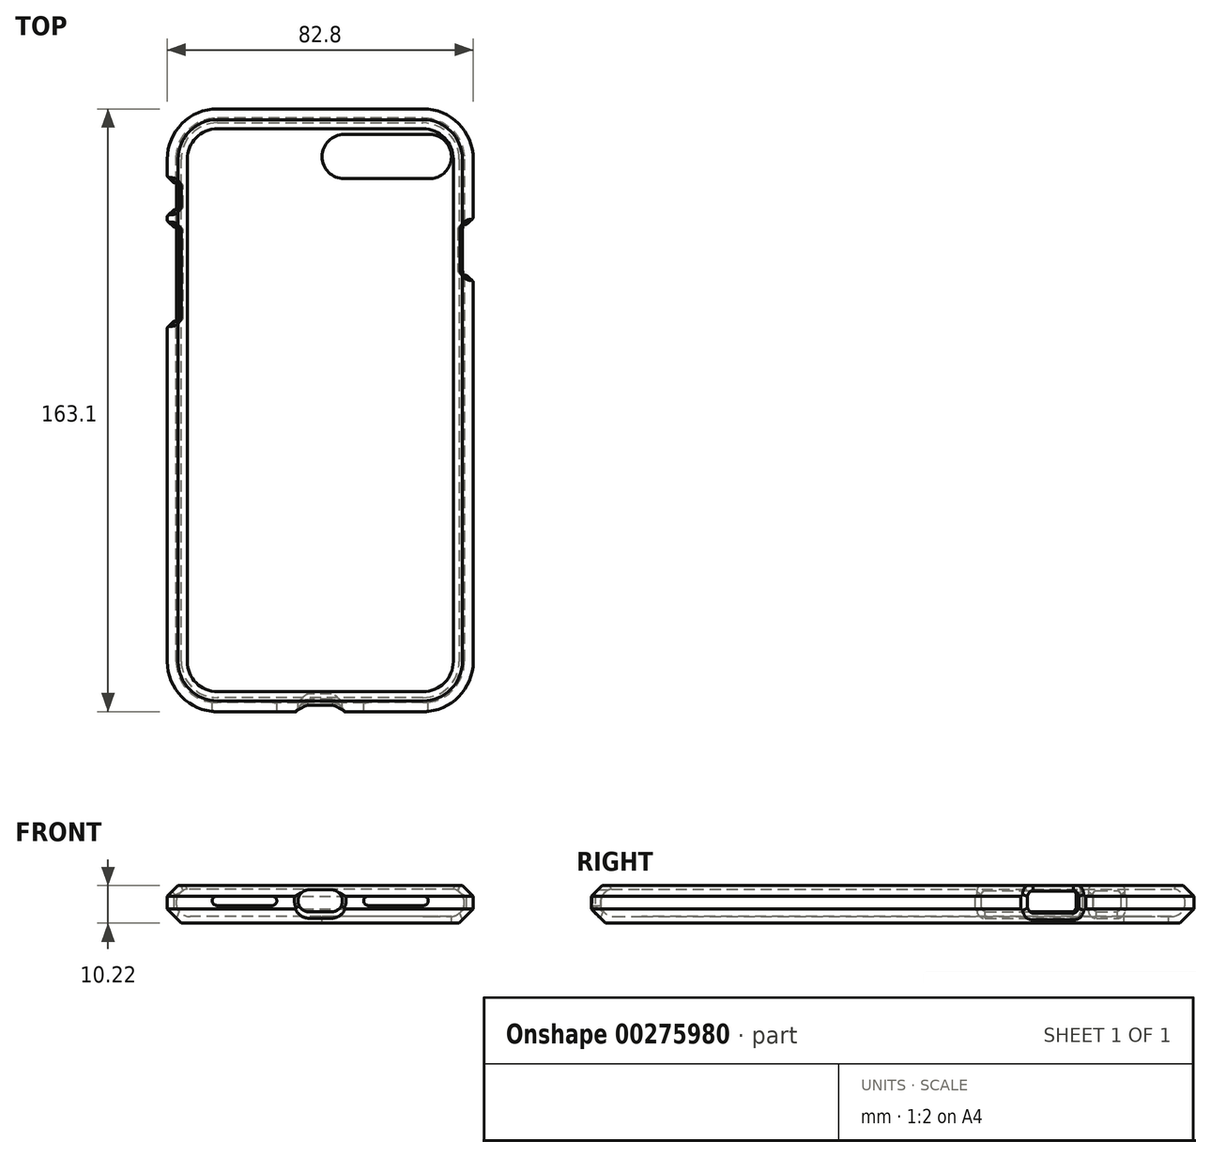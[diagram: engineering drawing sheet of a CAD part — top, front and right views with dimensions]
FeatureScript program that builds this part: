
annotation { "Feature Type Name" : "Feature", "Feature Type Description" : "" }
export const myFeature = defineFeature(function(context is Context, id is Id, definition is map)
    precondition{}
    {
        {
            assignVariable(context, id + "F0", {"name" : "HoleChamferLength", "anyValue" : 1.25});
        }
        {
            assignVariable(context, id + "F1", {"name" : "HoleChamferTopBottom", "anyValue" : 1.75});
        }
        {
            var Q0;
            Q0=qCreatedBy(makeId("Top.planeOp"),FACE);
            var sketch = newSketch(context, id + "F2", { "sketchPlane" : qUnion([Q0])});
            skLineSegment(sketch, "E0.bottom", {"start": v(27.8, 79.15) * mm, "end": v(0, 79.15) * mm});
            skLineSegment(sketch, "E0.top", {"start": v(27.8, -79.15) * mm, "end": v(-27.8, -79.15) * mm});
            skLineSegment(sketch, "E0.left", {"start": v(39, 67.95) * mm, "end": v(39, -67.95) * mm});
            skLineSegment(sketch, "E0.right", {"start": v(-39, 67.95) * mm, "end": v(-39, -67.95) * mm});
            skPoint(sketch, "E0.middle", {"position": v(0, 0) * mm});
            skPoint(sketch, "E1.visualSharp", {"position": v(-39, 79.15) * mm});
            skArc(sketch, "E1.filletArc", {"start": v(-27.8, 79.15) * mm, "mid": v(-35.72, 75.87) * mm, "end": v(-39, 67.95) * mm});
            skPoint(sketch, "E2.visualSharp", {"position": v(39, 79.15) * mm});
            skArc(sketch, "E2.filletArc", {"start": v(39, 67.95) * mm, "mid": v(35.72, 75.87) * mm, "end": v(27.8, 79.15) * mm});
            skPoint(sketch, "E3.visualSharp", {"position": v(39, -79.15) * mm});
            skArc(sketch, "E3.filletArc", {"start": v(27.8, -79.15) * mm, "mid": v(35.72, -75.87) * mm, "end": v(39, -67.95) * mm});
            skPoint(sketch, "E4.visualSharp", {"position": v(-39, -79.15) * mm});
            skArc(sketch, "E4.filletArc", {"start": v(-39, -67.95) * mm, "mid": v(-35.72, -75.87) * mm, "end": v(-27.8, -79.15) * mm});
            skLineSegment(sketch, "E5", {"start": v(0, 79.15) * mm, "end": v(-27.8, 79.15) * mm});
            skSolve(sketch);
        }
        {
            var Q0;
            Q0=qCreatedBy(makeId("Right.planeOp"),FACE);
            var sketch = newSketch(context, id + "F3", { "sketchPlane" : qUnion([Q0])});
            skPoint(sketch, "E6.0", {"position": v(79.15, 0) * mm});
            skArc(sketch, "E7", {"start": v(75.4, -3.75) * mm, "mid": v(79.15, 0) * mm, "end": v(75.4, 3.75) * mm});
            skLineSegment(sketch, "E8", {"start": v(75.4, -3.75) * mm, "end": v(75.4, 3.75) * mm, "construction": true});
            skLineSegment(sketch, "E9", {"start": v(81.55, -1.75) * mm, "end": v(81.55, 1.75) * mm});
            skLineSegment(sketch, "E10", {"start": v(81.55, 1.75) * mm, "end": v(79.77, 3.53) * mm});
            skLineSegment(sketch, "E11.trimOffspring", {"start": v(79.77, -3.53) * mm, "end": v(81.55, -1.75) * mm});
            skLineSegment(sketch, "E12", {"start": v(75.4, -5.55) * mm, "end": v(75.4, -3.75) * mm});
            skLineSegment(sketch, "E13", {"start": v(75.4, -5.55) * mm, "end": v(84.8, -5.55) * mm, "construction": true});
            skPoint(sketch, "E14", {"position": v(81.55, 0) * mm});
            skPoint(sketch, "E15.visualSharp", {"position": v(66.64, 4.65) * mm});
            skArc(sketch, "E15.filletArc", {"start": v(77.37, 4.67) * mm, "mid": v(76.58, 4.4) * mm, "end": v(76.15, 3.67) * mm});
            skLineSegment(sketch, "E16", {"start": v(79.77, -3.53) * mm, "end": v(77.75, -5.55) * mm});
            skLineSegment(sketch, "E17", {"start": v(77.75, -5.55) * mm, "end": v(75.4, -5.55) * mm});
            skLineSegment(sketch, "E18", {"start": v(79.77, 3.53) * mm, "end": v(78.63, 4.67) * mm});
            skLineSegment(sketch, "E19", {"start": v(78.63, 4.67) * mm, "end": v(77.37, 4.67) * mm});
            skLineSegment(sketch, "E20", {"start": v(76.15, 3.67) * mm, "end": v(68.38, 5.26) * mm, "construction": true});
            skSolve(sketch);
        }
        {
            var Q0;
            Q0=sQuery(id+"F2.wireOp",EDGE,"E5");
            var Q1;
            Q1=sQuery(id+"F2.wireOp",VERTEX,"E5.end");
            cPlane(context, id + "F4", {"entities" : qUnion([Q0, Q1]), "cplaneType" : CPlaneType.LINE_POINT, "offset" : 25 * mm, "width" : 150 * mm, "height" : 150 * mm});
        }
        {
            var Q0;
            Q0=sQuery(id+"F2.wireOp",EDGE,"E0.bottom");
            var Q1;
            Q1=sQuery(id+"F2.wireOp",VERTEX,"E2.filletArc.end");
            cPlane(context, id + "F5", {"entities" : qUnion([Q0, Q1]), "cplaneType" : CPlaneType.LINE_POINT, "offset" : 25 * mm, "width" : 150 * mm, "height" : 150 * mm});
        }
        {
            var Q0;
            Q0=sQuery(id+"F2.wireOp",EDGE,"E0.right");
            var Q1;
            Q1=sQuery(id+"F2.wireOp",VERTEX,"E0.right.end");
            cPlane(context, id + "F6", {"entities" : qUnion([Q0, Q1]), "cplaneType" : CPlaneType.LINE_POINT, "offset" : 25 * mm, "width" : 150 * mm, "height" : 150 * mm});
        }
        {
            var Q0;
            Q0=qCreatedBy(id+"F4.planeOp",FACE);
            var sketch = newSketch(context, id + "F7", { "sketchPlane" : qUnion([Q0])});
            skLineSegment(sketch, "E21.bottom", {"start": v(-25, -2.13) * mm, "end": v(-48.65, -2.13) * mm});
            skLineSegment(sketch, "E21.top", {"start": v(-25, 3.12) * mm, "end": v(-48.65, 3.12) * mm});
            skLineSegment(sketch, "E21.left", {"start": v(-24, -1.13) * mm, "end": v(-24, 2.12) * mm});
            skLineSegment(sketch, "E21.right", {"start": v(-49.65, -1.13) * mm, "end": v(-49.65, 2.12) * mm});
            skPoint(sketch, "E21.middle", {"position": v(-36.82, 0.5) * mm});
            skPoint(sketch, "E22.visualSharp", {"position": v(-49.65, 3.12) * mm});
            skArc(sketch, "E22.filletArc", {"start": v(-48.65, 3.12) * mm, "mid": v(-49.36, 2.83) * mm, "end": v(-49.65, 2.12) * mm});
            skPoint(sketch, "E23.visualSharp", {"position": v(-49.65, -2.13) * mm});
            skArc(sketch, "E23.filletArc", {"start": v(-49.65, -1.13) * mm, "mid": v(-49.36, -1.83) * mm, "end": v(-48.65, -2.13) * mm});
            skPoint(sketch, "E24.visualSharp", {"position": v(-24, 3.12) * mm});
            skArc(sketch, "E24.filletArc", {"start": v(-24, 2.12) * mm, "mid": v(-24.3, 2.83) * mm, "end": v(-25, 3.12) * mm});
            skPoint(sketch, "E25.visualSharp", {"position": v(-24, -2.12) * mm});
            skArc(sketch, "E25.filletArc", {"start": v(-25, -2.12) * mm, "mid": v(-24.3, -1.83) * mm, "end": v(-24, -1.13) * mm});
            skLineSegment(sketch, "E26.bottom", {"start": v(-60.65, 3.12) * mm, "end": v(-55.15, 3.12) * mm});
            skLineSegment(sketch, "E26.top", {"start": v(-60.65, -2.13) * mm, "end": v(-55.15, -2.13) * mm});
            skLineSegment(sketch, "E26.left", {"start": v(-61.65, 2.12) * mm, "end": v(-61.65, -1.13) * mm});
            skLineSegment(sketch, "E26.right", {"start": v(-54.15, 2.12) * mm, "end": v(-54.15, -1.13) * mm});
            skPoint(sketch, "E26.middle", {"position": v(-57.9, 0.5) * mm});
            skPoint(sketch, "E27.visualSharp", {"position": v(-61.65, 3.12) * mm});
            skArc(sketch, "E27.filletArc", {"start": v(-60.65, 3.13) * mm, "mid": v(-61.36, 2.83) * mm, "end": v(-61.65, 2.12) * mm});
            skPoint(sketch, "E28.visualSharp", {"position": v(-61.65, -2.13) * mm});
            skArc(sketch, "E28.filletArc", {"start": v(-61.65, -1.13) * mm, "mid": v(-61.36, -1.83) * mm, "end": v(-60.65, -2.13) * mm});
            skPoint(sketch, "E29.visualSharp", {"position": v(-54.15, -2.13) * mm});
            skArc(sketch, "E29.filletArc", {"start": v(-55.15, -2.13) * mm, "mid": v(-54.44, -1.83) * mm, "end": v(-54.15, -1.13) * mm});
            skPoint(sketch, "E30.visualSharp", {"position": v(-54.15, 3.12) * mm});
            skArc(sketch, "E30.filletArc", {"start": v(-54.15, 2.12) * mm, "mid": v(-54.44, 2.83) * mm, "end": v(-55.15, 3.13) * mm});
            skSolve(sketch);
        }
        {
            var Q0;
            Q0=qCreatedBy(id+"F5.planeOp",FACE);
            var sketch = newSketch(context, id + "F8", { "sketchPlane" : qUnion([Q0])});
            skLineSegment(sketch, "E31.bottom", {"start": v(-48.9, 3) * mm, "end": v(-37.9, 3) * mm});
            skLineSegment(sketch, "E31.top", {"start": v(-48.9, -2.5) * mm, "end": v(-37.9, -2.5) * mm});
            skLineSegment(sketch, "E31.left", {"start": v(-50.4, 1.5) * mm, "end": v(-50.4, -1) * mm});
            skLineSegment(sketch, "E31.right", {"start": v(-36.4, 1.5) * mm, "end": v(-36.4, -1) * mm});
            skPoint(sketch, "E31.middle", {"position": v(-43.4, 0.25) * mm});
            skPoint(sketch, "E32.visualSharp", {"position": v(-50.4, 3) * mm});
            skArc(sketch, "E32.filletArc", {"start": v(-48.9, 3) * mm, "mid": v(-49.96, 2.56) * mm, "end": v(-50.4, 1.5) * mm});
            skPoint(sketch, "E33.visualSharp", {"position": v(-50.4, -2.5) * mm});
            skArc(sketch, "E33.filletArc", {"start": v(-50.4, -1) * mm, "mid": v(-49.96, -2.06) * mm, "end": v(-48.9, -2.5) * mm});
            skPoint(sketch, "E34.visualSharp", {"position": v(-36.4, -2.5) * mm});
            skArc(sketch, "E34.filletArc", {"start": v(-37.9, -2.5) * mm, "mid": v(-36.84, -2.06) * mm, "end": v(-36.4, -1) * mm});
            skPoint(sketch, "E35.visualSharp", {"position": v(-36.4, 3) * mm});
            skArc(sketch, "E35.filletArc", {"start": v(-36.4, 1.5) * mm, "mid": v(-36.84, 2.56) * mm, "end": v(-37.9, 3) * mm});
            skSolve(sketch);
        }
        {
            var Q0;
            Q0=qCreatedBy(id+"F6.planeOp",FACE);
            var sketch = newSketch(context, id + "F9", { "sketchPlane" : qUnion([Q0])});
            skLineSegment(sketch, "E36.bottom", {"start": v(3, 3.5) * mm, "end": v(-3, 3.5) * mm});
            skLineSegment(sketch, "E36.top", {"start": v(3, -2.5) * mm, "end": v(-3, -2.5) * mm});
            skLineSegment(sketch, "E36.left", {"start": v(6, 0.5) * mm, "end": v(6, 0.5) * mm});
            skLineSegment(sketch, "E36.right", {"start": v(-6, 0.5) * mm, "end": v(-6, 0.5) * mm});
            skPoint(sketch, "E36.middle", {"position": v(0, 0.5) * mm});
            skPoint(sketch, "E37.visualSharp", {"position": v(-6, 3.5) * mm});
            skArc(sketch, "E37.filletArc", {"start": v(-3, 3.5) * mm, "mid": v(-5.12, 2.62) * mm, "end": v(-6, 0.5) * mm});
            skPoint(sketch, "E38.visualSharp", {"position": v(-6, -2.5) * mm});
            skArc(sketch, "E38.filletArc", {"start": v(-6, 0.5) * mm, "mid": v(-5.12, -1.62) * mm, "end": v(-3, -2.5) * mm});
            skPoint(sketch, "E39.visualSharp", {"position": v(6, -2.5) * mm});
            skArc(sketch, "E39.filletArc", {"start": v(3, -2.5) * mm, "mid": v(5.12, -1.62) * mm, "end": v(6, 0.5) * mm});
            skPoint(sketch, "E40.visualSharp", {"position": v(6, 3.5) * mm});
            skArc(sketch, "E40.filletArc", {"start": v(6, 0.5) * mm, "mid": v(5.12, 2.62) * mm, "end": v(3, 3.5) * mm});
            skLineSegment(sketch, "E41", {"start": v(13, 0.5) * mm, "end": v(28, 0.5) * mm, "construction": true});
            skArc(sketch, "E42.0.startCap", {"start": v(13, -0.75) * mm, "mid": v(11.75, 0.5) * mm, "end": v(13, 1.75) * mm});
            skArc(sketch, "E42.0.endCap", {"start": v(28, 1.75) * mm, "mid": v(29.25, 0.5) * mm, "end": v(28, -0.75) * mm});
            skLineSegment(sketch, "E42.0.left", {"start": v(13, 1.75) * mm, "end": v(28, 1.75) * mm});
            skLineSegment(sketch, "E42.0.right", {"start": v(13, -0.75) * mm, "end": v(28, -0.75) * mm});
            skLineSegment(sketch, "E43", {"start": v(0, 6.74) * mm, "end": v(0, -6.05) * mm, "construction": true});
            skLineSegment(sketch, "E44.MirrorCS", {"start": v(-13, -0.75) * mm, "end": v(-28, -0.75) * mm});
            skLineSegment(sketch, "E45.MirrorCS", {"start": v(-13, 1.75) * mm, "end": v(-28, 1.75) * mm});
            skArc(sketch, "E46.MirrorCS", {"start": v(-28, 1.75) * mm, "mid": v(-29.25, 0.5) * mm, "end": v(-28, -0.75) * mm});
            skArc(sketch, "E47.MirrorCS", {"start": v(-13, -0.75) * mm, "mid": v(-11.75, 0.5) * mm, "end": v(-13, 1.75) * mm});
            skLineSegment(sketch, "E48.MirrorCS", {"start": v(-13, 0.5) * mm, "end": v(-28, 0.5) * mm, "construction": true});
            skSolve(sketch);
        }
        {
            var Q0;
            Q0=qCreatedBy(makeId("Top.planeOp"),FACE);
            var sketch = newSketch(context, id + "F10", { "sketchPlane" : qUnion([Q0])});
            skLineSegment(sketch, "E49.bottom", {"start": v(29.5, 62.65) * mm, "end": v(6.5, 62.65) * mm});
            skLineSegment(sketch, "E49.top", {"start": v(29.5, 74.65) * mm, "end": v(6.5, 74.65) * mm});
            skLineSegment(sketch, "E49.left", {"start": v(35.5, 68.65) * mm, "end": v(35.5, 68.65) * mm});
            skLineSegment(sketch, "E49.right", {"start": v(0.5, 68.65) * mm, "end": v(0.5, 68.65) * mm});
            skPoint(sketch, "E49.middle", {"position": v(18, 68.65) * mm});
            skPoint(sketch, "E50.visualSharp", {"position": v(0.5, 74.65) * mm});
            skArc(sketch, "E50.filletArc", {"start": v(6.5, 74.65) * mm, "mid": v(2.26, 72.9) * mm, "end": v(0.5, 68.65) * mm});
            skPoint(sketch, "E51.visualSharp", {"position": v(0.5, 62.65) * mm});
            skArc(sketch, "E51.filletArc", {"start": v(0.5, 68.65) * mm, "mid": v(2.26, 64.4) * mm, "end": v(6.5, 62.65) * mm});
            skPoint(sketch, "E52.visualSharp", {"position": v(35.5, 62.65) * mm});
            skArc(sketch, "E52.filletArc", {"start": v(29.5, 62.65) * mm, "mid": v(33.74, 64.4) * mm, "end": v(35.5, 68.65) * mm});
            skPoint(sketch, "E53.visualSharp", {"position": v(35.5, 74.65) * mm});
            skArc(sketch, "E53.filletArc", {"start": v(35.5, 68.65) * mm, "mid": v(33.74, 72.9) * mm, "end": v(29.5, 74.65) * mm});
            skSolve(sketch);
        }
        {
            var Q0;
            Q0=qSketchRegion(id+"F3",true);
            var Q1;
            Q1=sQuery(id+"F2.wireOp",EDGE,"E5");
            var Q2;
            Q2=sQuery(id+"F2.wireOp",EDGE,"E1.filletArc");
            var Q3;
            Q3=sQuery(id+"F2.wireOp",EDGE,"E0.right");
            var Q4;
            Q4=sQuery(id+"F2.wireOp",EDGE,"E4.filletArc");
            var Q5;
            Q5=sQuery(id+"F2.wireOp",EDGE,"E0.top");
            var Q6;
            Q6=sQuery(id+"F2.wireOp",EDGE,"E3.filletArc");
            var Q7;
            Q7=sQuery(id+"F2.wireOp",EDGE,"E0.left");
            var Q8;
            Q8=sQuery(id+"F2.wireOp",EDGE,"E2.filletArc");
            var Q9;
            Q9=sQuery(id+"F2.wireOp",EDGE,"E0.bottom");
            sweep(context, id + "F11", {"profiles" : qUnion([Q0]), "path" : qUnion([Q1, Q2, Q3, Q4, Q5, Q6, Q7, Q8, Q9])});
        }
        {
            var Q0;
            Q0=qCreatedBy(makeId("Front.planeOp"),FACE);
            var sketch = newSketch(context, id + "F12", { "sketchPlane" : qUnion([Q0])});
            skLineSegment(sketch, "E54.0.0", {"start": v(35.25, -5.55) * mm, "end": v(27.8, -5.55) * mm});
            skLineSegment(sketch, "E54.0.1", {"start": v(27.8, -3.75) * mm, "end": v(27.8, -5.55) * mm});
            skLineSegment(sketch, "E54.0.2", {"start": v(27.8, -3.75) * mm, "end": v(35.25, -3.75) * mm});
            skLineSegment(sketch, "E54.0.3", {"start": v(35.25, -3.75) * mm, "end": v(35.25, -5.55) * mm});
            skLineSegment(sketch, "E54.1.0", {"start": v(27.8, -5.55) * mm, "end": v(-27.8, -5.55) * mm});
            skLineSegment(sketch, "E54.1.1", {"start": v(-27.8, -3.75) * mm, "end": v(-27.8, -5.55) * mm});
            skLineSegment(sketch, "E54.1.2", {"start": v(-27.8, -3.75) * mm, "end": v(27.8, -3.75) * mm});
            skLineSegment(sketch, "E54.1.3", {"start": v(27.8, -3.75) * mm, "end": v(27.8, -5.55) * mm});
            skLineSegment(sketch, "E54.2.0", {"start": v(-27.8, -5.55) * mm, "end": v(-35.25, -5.55) * mm});
            skLineSegment(sketch, "E54.2.1", {"start": v(-35.25, -3.75) * mm, "end": v(-35.25, -5.55) * mm});
            skLineSegment(sketch, "E54.2.2", {"start": v(-35.25, -3.75) * mm, "end": v(-27.8, -3.75) * mm});
            skLineSegment(sketch, "E54.2.3", {"start": v(-27.8, -3.75) * mm, "end": v(-27.8, -5.55) * mm});
            skSolve(sketch);
        }
        {
            var Q0;
            Q0=qSketchRegion(id+"F12",true);
            extrude(context, id + "F13", {"entities" : qUnion([Q0]), "operationType" : NewBodyOperationType.ADD, "endBound" : BoundingType.UP_TO_NEXT, "depth" : 25 * mm, "hasSecondDirection" : true, "secondDirectionBound" : SecondDirectionBoundingType.UP_TO_NEXT, "secondDirectionOppositeDirection" : true, "secondDirectionDepth" : 25 * mm});
        }
        {
            var Q0;
            Q0=qSketchRegion(id+"F7",true);
            extrude(context, id + "F14", {"entities" : qUnion([Q0]), "operationType" : NewBodyOperationType.REMOVE, "endBound" : BoundingType.THROUGH_ALL, "depth" : 25 * mm});
        }
        {
            var Q0;
            Q0=qSketchRegion(id+"F8",true);
            extrude(context, id + "F15", {"entities" : qUnion([Q0]), "operationType" : NewBodyOperationType.REMOVE, "endBound" : BoundingType.THROUGH_ALL, "oppositeDirection" : true, "depth" : 25 * mm});
        }
        {
            var Q0;
            Q0=makeQuery(id+"F10.imprint","IMPRINT",FACE,{"disambiguationData":[TD([[makeQuery(id+"F10.imprint","IMPRINT",EDGE,{"derivedFrom":sQuery(id+"F10.wireOp",EDGE,"E49.bottom")}),-1.0]])]});
            extrude(context, id + "F16", {"entities" : qUnion([Q0]), "operationType" : NewBodyOperationType.REMOVE, "endBound" : BoundingType.THROUGH_ALL, "oppositeDirection" : true, "depth" : 25 * mm});
        }
        {
            var Q0;
            Q0=qSketchRegion(id+"F9",true);
            extrude(context, id + "F17", {"entities" : qUnion([Q0]), "operationType" : NewBodyOperationType.REMOVE, "endBound" : BoundingType.THROUGH_ALL, "depth" : 25 * mm});
        }
        {
            var Q0;
            Q0=makeQuery(id+"F14.boolean.opBoolean","INTERSECT",EDGE,{"derivedFrom":[makeQuery(id+"F11.opSweep","SWEPT_FACE",FACE,{"disambiguationData":[OSD([sQuery(id+"F2.wireOp",EDGE,"E0.right"),sQuery(id+"F3.wireOp",EDGE,"E11.trimOffspring"),sQuery(id+"F3.wireOp",EDGE,"E16")])]}),makeQuery(id+"F14.opExtrude","SWEPT_FACE",FACE,{"disambiguationData":[OSD([sQuery(id+"F7.wireOp",EDGE,"E21.bottom")])]})]});
            var Q1;
            Q1=makeQuery(id+"F14.boolean.opBoolean","INTERSECT",EDGE,{"derivedFrom":[makeQuery(id+"F11.opSweep","SWEPT_FACE",FACE,{"disambiguationData":[OSD([sQuery(id+"F2.wireOp",EDGE,"E0.right"),sQuery(id+"F3.wireOp",EDGE,"E10")])]}),makeQuery(id+"F14.opExtrude","SWEPT_FACE",FACE,{"disambiguationData":[OSD([sQuery(id+"F7.wireOp",EDGE,"E21.top")])]})]});
            chamfer(context, id + "F18", {"entities" : qUnion([Q0, Q1]), "width" : (getVariable(context, 'HoleChamferLength')) * mm, "tangentPropagation" : true});
        }
        {
            var Q0;
            Q0=makeQuery(id+"F14.boolean.opBoolean","INTERSECT",EDGE,{"derivedFrom":[makeQuery(id+"F11.opSweep","SWEPT_FACE",FACE,{"disambiguationData":[OSD([sQuery(id+"F2.wireOp",EDGE,"E0.right"),sQuery(id+"F3.wireOp",EDGE,"E11.trimOffspring"),sQuery(id+"F3.wireOp",EDGE,"E16")])]}),makeQuery(id+"F14.opExtrude","SWEPT_FACE",FACE,{"disambiguationData":[OSD([sQuery(id+"F7.wireOp",EDGE,"E26.top")])]})]});
            var Q1;
            Q1=makeQuery(id+"F14.boolean.opBoolean","INTERSECT",EDGE,{"derivedFrom":[makeQuery(id+"F11.opSweep","SWEPT_FACE",FACE,{"disambiguationData":[OSD([sQuery(id+"F2.wireOp",EDGE,"E0.right"),sQuery(id+"F3.wireOp",EDGE,"E10")])]}),makeQuery(id+"F14.opExtrude","SWEPT_FACE",FACE,{"disambiguationData":[OSD([sQuery(id+"F7.wireOp",EDGE,"E26.bottom")])]})]});
            chamfer(context, id + "F19", {"entities" : qUnion([Q0, Q1]), "width" : (getVariable(context, 'HoleChamferLength')) * mm, "tangentPropagation" : true});
        }
        {
            var Q0;
            Q0=makeQuery(id+"F15.boolean.opBoolean","INTERSECT",EDGE,{"derivedFrom":[makeQuery(id+"F11.opSweep","SWEPT_FACE",FACE,{"disambiguationData":[OSD([sQuery(id+"F2.wireOp",EDGE,"E0.left"),sQuery(id+"F3.wireOp",EDGE,"E11.trimOffspring"),sQuery(id+"F3.wireOp",EDGE,"E16")])]}),makeQuery(id+"F15.opExtrude","SWEPT_FACE",FACE,{"disambiguationData":[OSD([sQuery(id+"F8.wireOp",EDGE,"E31.top")])]})]});
            var Q1;
            Q1=makeQuery(id+"F15.boolean.opBoolean","INTERSECT",EDGE,{"derivedFrom":[makeQuery(id+"F11.opSweep","SWEPT_FACE",FACE,{"disambiguationData":[OSD([sQuery(id+"F2.wireOp",EDGE,"E0.left"),sQuery(id+"F3.wireOp",EDGE,"E10")])]}),makeQuery(id+"F15.opExtrude","SWEPT_FACE",FACE,{"disambiguationData":[OSD([sQuery(id+"F8.wireOp",EDGE,"E31.bottom")])]})]});
            chamfer(context, id + "F20", {"entities" : qUnion([Q0, Q1]), "width" : (getVariable(context, 'HoleChamferLength')) * mm, "tangentPropagation" : true});
        }
        {
            var Q0;
            Q0=makeQuery(id+"F15.boolean.opBoolean","INTERSECT",EDGE,{"derivedFrom":[makeQuery(id+"F11.opSweep","SWEPT_FACE",FACE,{"disambiguationData":[OSD([sQuery(id+"F2.wireOp",EDGE,"E0.left"),sQuery(id+"F3.wireOp",EDGE,"E9")])]}),makeQuery(id+"F15.opExtrude","SWEPT_FACE",FACE,{"disambiguationData":[OSD([sQuery(id+"F8.wireOp",EDGE,"E31.left")])]})]});
            var Q1;
            Q1=makeQuery(id+"F15.boolean.opBoolean","INTERSECT",EDGE,{"derivedFrom":[makeQuery(id+"F11.opSweep","SWEPT_FACE",FACE,{"disambiguationData":[OSD([sQuery(id+"F2.wireOp",EDGE,"E0.left"),sQuery(id+"F3.wireOp",EDGE,"E9")])]}),makeQuery(id+"F15.opExtrude","SWEPT_FACE",FACE,{"disambiguationData":[OSD([sQuery(id+"F8.wireOp",EDGE,"E31.right")])]})]});
            var Q2;
            Q2=makeQuery(id+"F14.boolean.opBoolean","INTERSECT",EDGE,{"derivedFrom":[makeQuery(id+"F11.opSweep","SWEPT_FACE",FACE,{"disambiguationData":[OSD([sQuery(id+"F2.wireOp",EDGE,"E0.right"),sQuery(id+"F3.wireOp",EDGE,"E9")])]}),makeQuery(id+"F14.opExtrude","SWEPT_FACE",FACE,{"disambiguationData":[OSD([sQuery(id+"F7.wireOp",EDGE,"E21.left")])]})]});
            var Q3;
            Q3=makeQuery(id+"F14.boolean.opBoolean","INTERSECT",EDGE,{"derivedFrom":[makeQuery(id+"F11.opSweep","SWEPT_FACE",FACE,{"disambiguationData":[OSD([sQuery(id+"F2.wireOp",EDGE,"E0.right"),sQuery(id+"F3.wireOp",EDGE,"E9")])]}),makeQuery(id+"F14.opExtrude","SWEPT_FACE",FACE,{"disambiguationData":[OSD([sQuery(id+"F7.wireOp",EDGE,"E21.right")])]})]});
            var Q4;
            Q4=makeQuery(id+"F14.boolean.opBoolean","INTERSECT",EDGE,{"derivedFrom":[makeQuery(id+"F11.opSweep","SWEPT_FACE",FACE,{"disambiguationData":[OSD([sQuery(id+"F2.wireOp",EDGE,"E0.right"),sQuery(id+"F3.wireOp",EDGE,"E9")])]}),makeQuery(id+"F14.opExtrude","SWEPT_FACE",FACE,{"disambiguationData":[OSD([sQuery(id+"F7.wireOp",EDGE,"E26.left")])]})]});
            var Q5;
            Q5=makeQuery(id+"F14.boolean.opBoolean","INTERSECT",EDGE,{"derivedFrom":[makeQuery(id+"F11.opSweep","SWEPT_FACE",FACE,{"disambiguationData":[OSD([sQuery(id+"F2.wireOp",EDGE,"E0.right"),sQuery(id+"F3.wireOp",EDGE,"E9")])]}),makeQuery(id+"F14.opExtrude","SWEPT_FACE",FACE,{"disambiguationData":[OSD([sQuery(id+"F7.wireOp",EDGE,"E26.right")])]})]});
            chamfer(context, id + "F21", {"entities" : qUnion([Q0, Q1, Q2, Q3, Q4, Q5]), "width" : (getVariable(context, 'HoleChamferTopBottom')) * mm, "tangentPropagation" : true});
        }
        {
            var Q0;
            Q0=makeQuery(id+"F17.boolean.opBoolean","INTERSECT",EDGE,{"derivedFrom":[makeQuery(id+"F11.opSweep","SWEPT_FACE",FACE,{"disambiguationData":[OSD([sQuery(id+"F2.wireOp",EDGE,"E0.top"),sQuery(id+"F3.wireOp",EDGE,"E11.trimOffspring"),sQuery(id+"F3.wireOp",EDGE,"E16")])]}),makeQuery(id+"F17.opExtrude","SWEPT_FACE",FACE,{"disambiguationData":[OSD([sQuery(id+"F9.wireOp",EDGE,"E36.top")])]})]});
            var Q1;
            Q1=makeQuery(id+"F17.boolean.opBoolean","INTERSECT",EDGE,{"derivedFrom":[makeQuery(id+"F11.opSweep","SWEPT_FACE",FACE,{"disambiguationData":[OSD([sQuery(id+"F2.wireOp",EDGE,"E0.top"),sQuery(id+"F3.wireOp",EDGE,"E9")])]}),makeQuery(id+"F17.opExtrude","SWEPT_FACE",FACE,{"disambiguationData":[OSD([sQuery(id+"F9.wireOp",EDGE,"E37.filletArc"),sQuery(id+"F9.wireOp",EDGE,"E38.filletArc")])]})]});
            var Q2;
            Q2=makeQuery(id+"F17.boolean.opBoolean","INTERSECT",EDGE,{"derivedFrom":[makeQuery(id+"F11.opSweep","SWEPT_FACE",FACE,{"disambiguationData":[OSD([sQuery(id+"F2.wireOp",EDGE,"E0.top"),sQuery(id+"F3.wireOp",EDGE,"E9")])]}),makeQuery(id+"F17.opExtrude","SWEPT_FACE",FACE,{"disambiguationData":[OSD([sQuery(id+"F9.wireOp",EDGE,"E39.filletArc"),sQuery(id+"F9.wireOp",EDGE,"E40.filletArc")])]})]});
            chamfer(context, id + "F22", {"entities" : qUnion([Q0, Q1, Q2]), "width" : 1 * mm, "tangentPropagation" : true});
        }
    });
